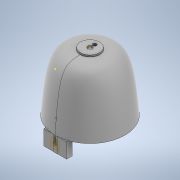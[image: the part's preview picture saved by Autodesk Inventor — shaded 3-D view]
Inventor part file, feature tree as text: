
AUTODESK INVENTOR PART (.ipt)
format: ipt  version: 2021.1 (Build 251245010, 245A)  size: 529,408 bytes
history: native  units: mm
features: sketch x11, extrude x7, plane x5, mirror x5, revolve x1, hole x1, thread x1
ambient origin geometry x8: Origin, YZ Plane, XZ Plane, XY Plane, X Axis, Y Axis, Z Axis, Center Point
bodies: Solid1 (feature_tree)
feature tree (31):
  extrude  "Extrusion1"  TaperAngle=0.0deg  [1 undecoded]
  plane  "Work Plane2"
  revolve  "Revolution1"  [1 undecoded]
  mirror  "Mirror1"
  plane  "Work Plane3"
  hole  "Hole1"  [1 undecoded]
  thread  "Thread1"  [1 undecoded]
  extrude  "Extrusion2"  Depth=178.334mm TaperAngle=0.0deg
  mirror  "Mirror2"
  extrude  "Extrusion4"  Depth=10.0mm
  sketch  "Sketch9"  dims[d36=0.0mm d40=10.0mm]
  plane  "Work Plane4"
  extrude  "Extrusion5"  Depth=25.0mm
  mirror  "Mirror4"
  extrude  "Extrusion6"  Depth=55.0mm
  sketch  "Sketch12"  dims[d46=5.0mm d49=12.0mm]
  mirror  "Mirror5"
  sketch  "Sketch13"  dims[d50=0.0mm d51=14.5mm]
  plane  "Work Plane5"
  extrude  "Extrusion7"  Depth=12.0mm
  mirror  "Mirror6"
  extrude  "Extrusion8"  Depth=14.5mm
  plane  "Work Plane1"
  sketch  "Sketch3"  dims[d1=50.0mm d3=0.0mm]
  sketch  "Sketch4"  dims[d4=25.0mm d5=-50.0mm d9=15.0mm]
  sketch  "Sketch6"  dims[d10=15.0mm d11=360.0deg d12=92.0455mm]
  sketch  "Sketch8"  dims[d16=3.0mm d17=6.0mm d18=4.0mm d19=2.0mm d20=90.0deg d21=8.0mm d22=20.594885mm d23=178.334mm d24=0.0mm]
  sketch  "Sketch10"  dims[d41=0.0mm d42=0.0mm d43=25.0mm]
  sketch  "Sketch11"  dims[d44=5.0mm d45=55.0mm]
  sketch  "Sketch14"  dims[d56=6.8mm]
  sketch  "Sketch15"  dims[d57=1.5mm d58=12.0mm d59=0.0mm d60=14.5mm d61=10.0mm d62=0.0mm d63=90.0deg d65=1.0mm d66=0.0mm d68=0.0mm d69=0.0mm d70=3.0mm]
note: 4 required parameter values undecoded (feature->parameter linkage not recoverable at this tier; creation-order binding heuristic only, values carry confidence <= 0.55)